# Revit family: Sanitary_Bidets_DURAVIT-AG_D-Neo-Floor-mounted-bidet-White-High-Gloss-650 mm-229410
name_source: partatom
category: Plumbing Fixtures
revit_build: Autodesk Revit 2018 (Build: 20190510_1515(x64)
units: mm (PartAtom-declared; Revit-internal decimal feet)

## family parameters
Always vertical = No
Cut with Voids When Loaded = No
OmniClass Number = 23.31.23.00
OmniClass Title = Bidets
Part Type = Normal
Room Calculation Point = No
Round Connector Dimension = Use Diameter
Shared = No
Work Plane-Based = Yes

## types (1)
- D-Neo Floor-mounted bidet White High Gloss 650 mm - 229410
    Always visible = Yes
    BIMobject category = Bidets
    Date of publishing = 05.05.2021 00:00:00
    Default Elevation = 1219.2 mm  [stored 4 ft]
    Description = D-Neo offers sophisticated and holistic bathroom design at an entry-level price. The concept of the Belgian designer Bertrand Lejoly makes an impression with its clear design and hence fits into any room without being subsumed. The floorstanding bidet is the perfect complement to the D-Neo pedestal toilet.
    Diameter = 31.75 mm
    Edition number = 1
    IFC Classification = Sanitary Terminal
    Installation instructions = https://duravit-public-assets.s3.eu-central-1.amazonaws.com
    Main material = Duravit - Ceramic - 00 - White Alpin
    Manufacturer = Duravit
    Manufacturer name = DURAVIT AG
    Masterformat 2014 Code = 22 41 13.19
    Masterformat 2014 Description = Residential Bidets
    Material main = Ceramics
    Model = D-Neo Floor-mounted bidet White High Gloss 650 mm - 229410
    NBS Reference Code = 35-06-11
    NBS Reference Description = Bidets
    OmniClass Code = 23-31 23 00
    OmniClass Description = Bidets
    Product Guid = 9cf06833-2df3-4183-8675-f25ed285c3c2
    Product SKU = d-neo-floor-mounted-bidet-229410
    Product data url = https://bimobject.com
    Product family = D-Neo
    Product group = Floor-mounted bidet
    Product name = D-Neo Floor-mounted bidet White High Gloss 650 mm - 229410
    QR code = https://bimobject.com
    UNSPSC Code = 30181502
    URL = https://www.duravit.com
    Uniclass 1.4 Code = L7215
    Uniclass 1.4 Description = Bidets
    Uniclass 2.0 Code = PR-35-06-11
    Uniclass 2.0 Description = Bidets
    Uniclass 2015 Code = Pr_40_20_06_11
    Uniclass 2015 Name = Bidets
    Uniformat II Code = D2010
    Uniformat II Description = Plumbing Fixtures
    Weight Net (Kg) = 35,7

note: [stored X ft] marks values corroborated as IEEE doubles in the binary element streams (Revit-internal decimal feet)

## geometry (parser evidence)
native form markers: Sweep x3
no freeform markers — native parametric forms only
